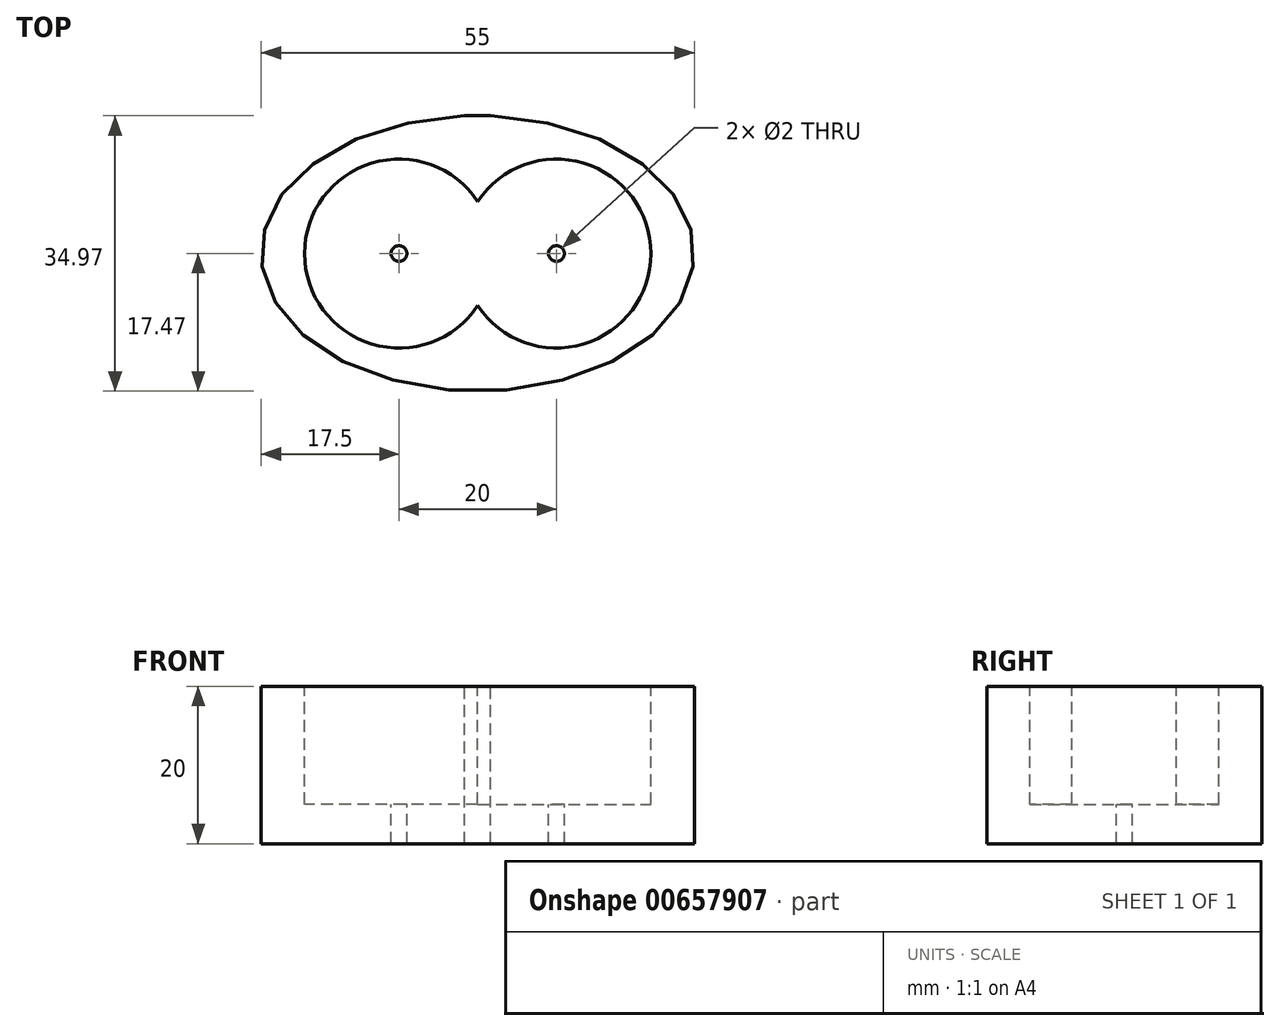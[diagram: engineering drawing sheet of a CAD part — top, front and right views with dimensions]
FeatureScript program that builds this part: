
annotation { "Feature Type Name" : "Feature", "Feature Type Description" : "" }
export const myFeature = defineFeature(function(context is Context, id is Id, definition is map)
    precondition{}
    {
        {
            var Q0;
            Q0=qCreatedBy(makeId("Top.planeOp"),FACE);
            var sketch = newSketch(context, id + "F0", { "sketchPlane" : qUnion([Q0])});
            skLineSegment(sketch, "E0.bottom", {"start": v(0, 35) * mm, "end": v(55, 35) * mm});
            skLineSegment(sketch, "E0.top", {"start": v(0, 0) * mm, "end": v(55, 0) * mm});
            skLineSegment(sketch, "E0.left", {"start": v(0, 35) * mm, "end": v(0, 0) * mm});
            skLineSegment(sketch, "E0.right", {"start": v(55, 35) * mm, "end": v(55, 0) * mm});
            skSolve(sketch);
        }
        {
            var Q0;
            Q0 = qSketchRegion(id + "F0", true);
            var Q1;
            Q1=makeQuery(id+"F0.imprint","IMPRINT",FACE,{"disambiguationData":[TD([[makeQuery(id+"F0.imprint","IMPRINT",EDGE,{"derivedFrom":sQuery(id+"F0.wireOp",EDGE,"E0.bottom")}),-1.0]])]});
            extrude(context, id + "F1", {"entities" : qUnion([Q0, Q1]), "depth" : 20 * mm, "offsetDistance" : 25 * mm});
        }
        {
            var Q0;
            Q0=makeQuery(id+"F1.opExtrude","CAP_FACE",FACE,{"disambiguationData":[OSD([sQuery(id+"F0.wireOp",EDGE,"E0.bottom"),sQuery(id+"F0.wireOp",EDGE,"E0.top"),sQuery(id+"F0.wireOp",EDGE,"E0.left"),sQuery(id+"F0.wireOp",EDGE,"E0.right")])],"isStart":false});
            var sketch = newSketch(context, id + "F2", { "sketchPlane" : qUnion([Q0])});
            skCircle(sketch, "E1", {"center": v(17.5, 17.5) * mm, "radius": 12 * mm});
            skCircle(sketch, "E2", {"center": v(37.5, 17.5) * mm, "radius": 12 * mm});
            skCircle(sketch, "E3", {"center": v(17.5, 17.5) * mm, "radius": 1 * mm});
            skCircle(sketch, "E4", {"center": v(37.5, 17.5) * mm, "radius": 1 * mm});
            skSolve(sketch);
        }
        {
            var Q0;
            {var subQ0=sQuery(id+"F2.wireOp",EDGE,"E2");var subQ1=sQuery(id+"F2.wireOp",EDGE,"E1");var subQ2=makeQuery(id+"F2.imprint","INTERSECT",VERTEX,{"disambiguationData":[OD(0.0)],"derivedFrom":[subQ1,subQ0]});Q0=makeQuery(id+"F2.imprint","IMPRINT",FACE,{"disambiguationData":[TD([[makeQuery(id+"F2.imprint","IMPRINT",EDGE,{"disambiguationData":[TD([[subQ2,-1.0]])],"derivedFrom":subQ1}),-1.0]])]});}
            var Q1;
            {var subQ0=sQuery(id+"F2.wireOp",EDGE,"E2");var subQ1=sQuery(id+"F2.wireOp",EDGE,"E1");var subQ2=makeQuery(id+"F2.imprint","INTERSECT",VERTEX,{"disambiguationData":[OD(0.0)],"derivedFrom":[subQ1,subQ0]});Q1=makeQuery(id+"F2.imprint","IMPRINT",FACE,{"disambiguationData":[TD([[makeQuery(id+"F2.imprint","IMPRINT",EDGE,{"disambiguationData":[TD([[subQ2,1.0]])],"derivedFrom":subQ1}),1.0]])]});}
            var Q2;
            {var subQ0=sQuery(id+"F2.wireOp",EDGE,"E2");var subQ1=sQuery(id+"F2.wireOp",EDGE,"E1");var subQ2=makeQuery(id+"F2.imprint","INTERSECT",VERTEX,{"disambiguationData":[OD(0.0)],"derivedFrom":[subQ1,subQ0]});Q2=makeQuery(id+"F2.imprint","IMPRINT",FACE,{"disambiguationData":[TD([[makeQuery(id+"F2.imprint","IMPRINT",EDGE,{"disambiguationData":[TD([[subQ2,-1.0]])],"derivedFrom":subQ1}),1.0]])]});}
            extrude(context, id + "F3", {"entities" : qUnion([Q0, Q1, Q2]), "operationType" : NewBodyOperationType.REMOVE, "oppositeDirection" : true, "depth" : 15 * mm, "offsetDistance" : 25 * mm});
        }
        {
            var Q0;
            Q0=makeQuery(id+"F1.opExtrude","CAP_FACE",FACE,{"disambiguationData":[OSD([sQuery(id+"F0.wireOp",EDGE,"E0.bottom"),sQuery(id+"F0.wireOp",EDGE,"E0.top"),sQuery(id+"F0.wireOp",EDGE,"E0.left"),sQuery(id+"F0.wireOp",EDGE,"E0.right")])],"isStart":false});
            var sketch = newSketch(context, id + "F4", { "sketchPlane" : qUnion([Q0])});
            skEllipse(sketch, "E5", {"center": v(27.5, 17.53) * mm, "majorRadius": 27.5 * mm, "minorRadius": 17.5 * mm, "majorAxis": v(1, 0)});
            skSolve(sketch);
        }
        {
            var Q0;
            {var subQ0=sQuery(id+"F4.wireOp",EDGE,"E5");var subQ1=makeQuery(id+"F1.opExtrude","CAP_EDGE",EDGE,{"disambiguationData":[OSD([sQuery(id+"F0.wireOp",EDGE,"E0.bottom")])],"isStart":false});var subQ2=makeQuery(id+"F4.imprint","INTERSECT",VERTEX,{"disambiguationData":[OD(1.0)],"derivedFrom":[subQ1,subQ0]});Q0=makeQuery(id+"F4.imprint","IMPRINT",FACE,{"disambiguationData":[TD([[makeQuery(id+"F4.imprint","IMPRINT",EDGE,{"disambiguationData":[TD([[subQ2,-1.0]])],"derivedFrom":subQ0}),-1.0]])]});}
            var Q1;
            {var subQ0=sQuery(id+"F4.wireOp",EDGE,"E5");var subQ1=makeQuery(id+"F1.opExtrude","CAP_EDGE",EDGE,{"disambiguationData":[OSD([sQuery(id+"F0.wireOp",EDGE,"E0.bottom")])],"isStart":false});var subQ2=makeQuery(id+"F4.imprint","INTERSECT",VERTEX,{"disambiguationData":[OD(0.0)],"derivedFrom":[subQ1,subQ0]});Q1=makeQuery(id+"F4.imprint","IMPRINT",FACE,{"disambiguationData":[TD([[makeQuery(id+"F4.imprint","IMPRINT",EDGE,{"disambiguationData":[TD([[subQ2,1.0]])],"derivedFrom":subQ0}),-1.0]])]});}
            var Q2;
            {var subQ5=makeQuery(id+"F1.opExtrude","CAP_EDGE",EDGE,{"disambiguationData":[OSD([sQuery(id+"F0.wireOp",EDGE,"E0.top")])],"isStart":false});Q2=makeQuery(id+"F4.imprint","IMPRINT",FACE,{"disambiguationData":[TD([[makeQuery(id+"F4.imprint","IMPRINT",EDGE,{"derivedFrom":subQ5}),1.0]])]});}
            extrude(context, id + "F5", {"entities" : qUnion([Q0, Q1, Q2]), "operationType" : NewBodyOperationType.REMOVE, "oppositeDirection" : true, "depth" : 25 * mm, "offsetDistance" : 25 * mm});
        }
        {
            var Q0;
            Q0=makeQuery(id+"F3.boolean.opBoolean","SPLIT",FACE,{"disambiguationData":[TD([makeQuery(id+"F3.opExtrude","SWEPT_FACE",FACE,{"disambiguationData":[OSD([sQuery(id+"F2.wireOp",EDGE,"E4")])]})])],"derivedFrom":makeQuery(id+"F1.opExtrude","CAP_FACE",FACE,{"disambiguationData":[OSD([sQuery(id+"F0.wireOp",EDGE,"E0.bottom"),sQuery(id+"F0.wireOp",EDGE,"E0.top"),sQuery(id+"F0.wireOp",EDGE,"E0.left"),sQuery(id+"F0.wireOp",EDGE,"E0.right")])],"isStart":false})});
            var Q1;
            Q1=makeQuery(id+"F3.boolean.opBoolean","SPLIT",FACE,{"disambiguationData":[TD([makeQuery(id+"F3.opExtrude","SWEPT_FACE",FACE,{"disambiguationData":[OSD([sQuery(id+"F2.wireOp",EDGE,"E3")])]})])],"derivedFrom":makeQuery(id+"F1.opExtrude","CAP_FACE",FACE,{"disambiguationData":[OSD([sQuery(id+"F0.wireOp",EDGE,"E0.bottom"),sQuery(id+"F0.wireOp",EDGE,"E0.top"),sQuery(id+"F0.wireOp",EDGE,"E0.left"),sQuery(id+"F0.wireOp",EDGE,"E0.right")])],"isStart":false})});
            extrude(context, id + "F6", {"entities" : qUnion([Q0, Q1]), "operationType" : NewBodyOperationType.REMOVE, "oppositeDirection" : true, "depth" : 20 * mm, "offsetDistance" : 25 * mm});
        }
    });
